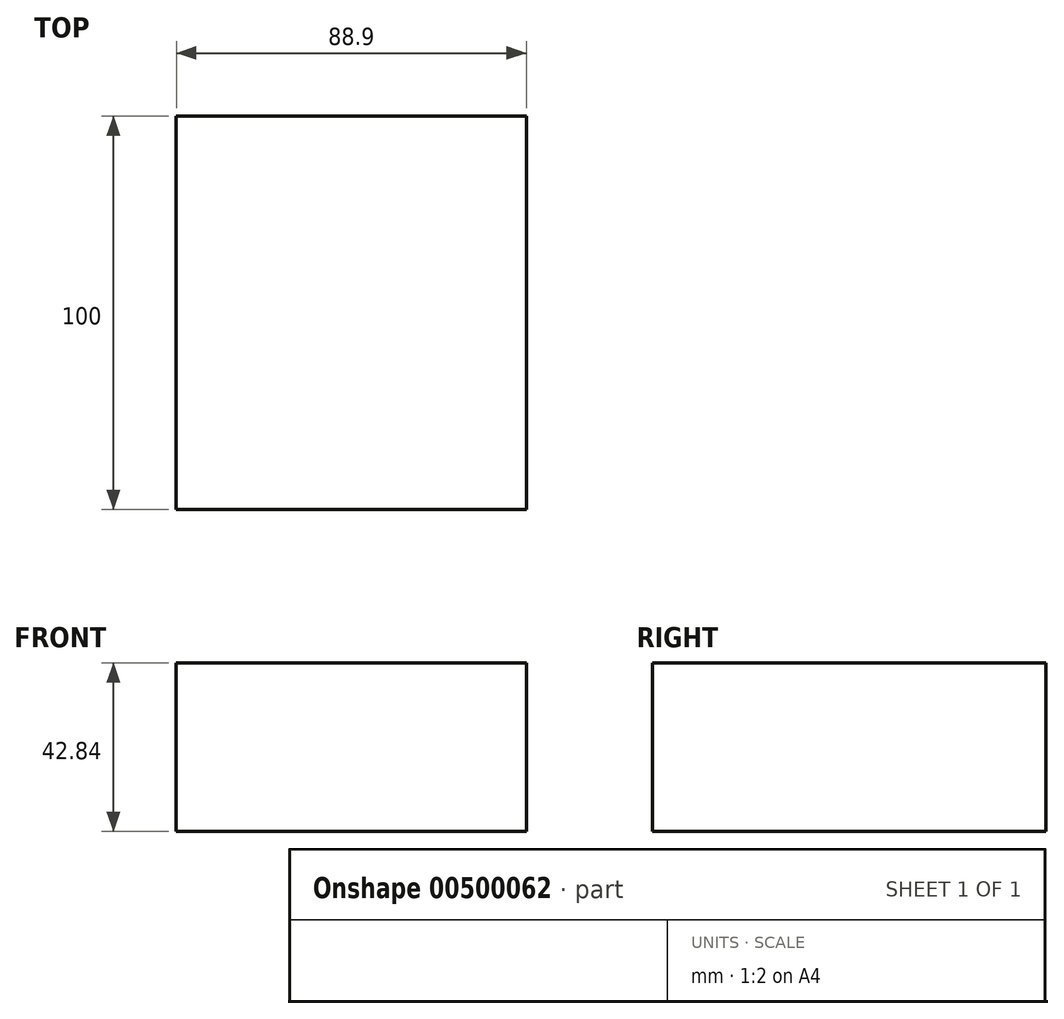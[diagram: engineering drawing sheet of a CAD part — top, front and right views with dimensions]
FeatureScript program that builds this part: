
annotation { "Feature Type Name" : "Feature", "Feature Type Description" : "" }
export const myFeature = defineFeature(function(context is Context, id is Id, definition is map)
    precondition{}
    {
        {
            var Q0;
            Q0=qCreatedBy(makeId("Front.planeOp"),FACE);
            var sketch = newSketch(context, id + "F0", { "sketchPlane" : qUnion([Q0])});
            skLineSegment(sketch, "E0.bottom", {"start": v(-41.97, 27.25) * mm, "end": v(46.93, 27.25) * mm});
            skLineSegment(sketch, "E0.top", {"start": v(-41.97, -15.6) * mm, "end": v(46.93, -15.6) * mm});
            skLineSegment(sketch, "E0.left", {"start": v(-41.97, 27.25) * mm, "end": v(-41.97, -15.6) * mm});
            skLineSegment(sketch, "E0.right", {"start": v(46.93, 27.25) * mm, "end": v(46.93, -15.6) * mm});
            skSolve(sketch);
        }
        {
            var Q0;
            Q0=makeQuery(id+"F0.imprint","IMPRINT",FACE,{"disambiguationData":[TD([[makeQuery(id+"F0.imprint","IMPRINT",EDGE,{"derivedFrom":sQuery(id+"F0.wireOp",EDGE,"E0.bottom")}),-1.0]])]});
            extrude(context, id + "F1", {"entities" : qUnion([Q0]), "depth" : 100 * mm, "symmetric" : true});
        }
    });
